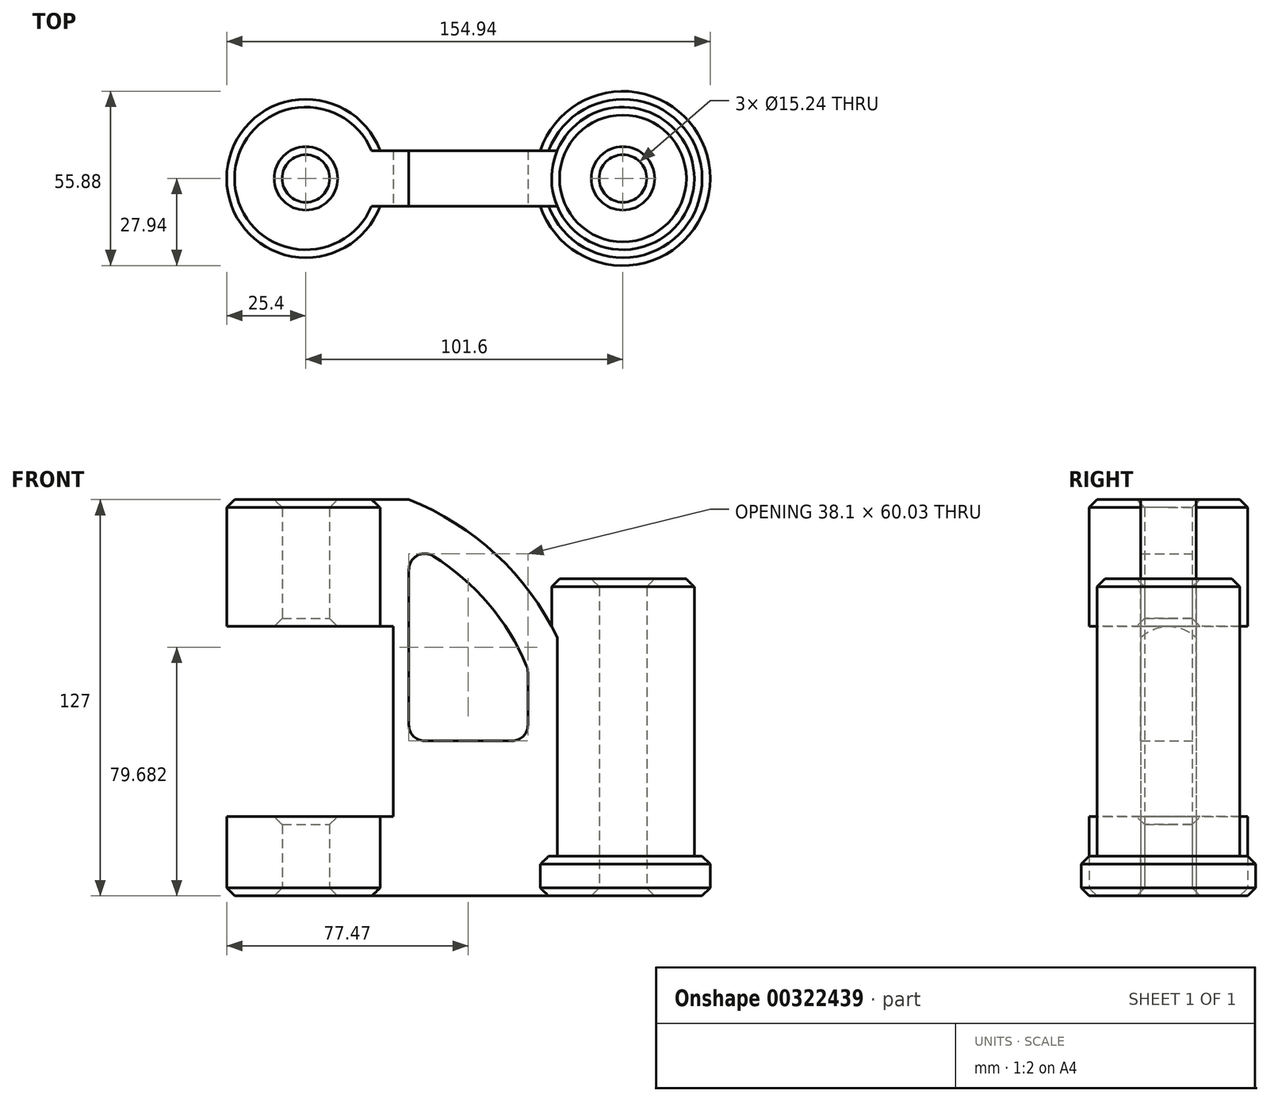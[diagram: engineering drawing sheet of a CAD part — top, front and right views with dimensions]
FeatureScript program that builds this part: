
annotation { "Feature Type Name" : "Feature", "Feature Type Description" : "" }
export const myFeature = defineFeature(function(context is Context, id is Id, definition is map)
    precondition{}
    {
        {
            var Q0;
            Q0=qCreatedBy(makeId("Top.planeOp"),FACE);
            var sketch = newSketch(context, id + "F0", { "sketchPlane" : qUnion([Q0])});
            skCircle(sketch, "E0", {"center": v(0, 0) * mm, "radius": 25.4 * mm});
            skCircle(sketch, "E1", {"center": v(0, 0) * mm, "radius": 7.62 * mm});
            skCircle(sketch, "E2", {"center": v(101.6, 0) * mm, "radius": 22.86 * mm});
            skCircle(sketch, "E3", {"center": v(101.6, 0) * mm, "radius": 7.62 * mm});
            skSolve(sketch);
        }
        {
            var Q0;
            Q0=makeQuery(id+"F0.imprint","IMPRINT",FACE,{"disambiguationData":[TD([[makeQuery(id+"F0.imprint","IMPRINT",EDGE,{"derivedFrom":sQuery(id+"F0.wireOp",EDGE,"E0")}),1.0]])]});
            extrude(context, id + "F1", {"entities" : qUnion([Q0]), "depth" : 127 * mm});
        }
        {
            var Q0;
            Q0=makeQuery(id+"F0.imprint","IMPRINT",FACE,{"disambiguationData":[TD([[makeQuery(id+"F0.imprint","IMPRINT",EDGE,{"derivedFrom":sQuery(id+"F0.wireOp",EDGE,"E2")}),1.0]])]});
            extrude(context, id + "F2", {"entities" : qUnion([Q0]), "depth" : 101.6 * mm});
        }
        {
            var Q0;
            Q0=qCreatedBy(makeId("Front.planeOp"),FACE);
            var sketch = newSketch(context, id + "F3", { "sketchPlane" : qUnion([Q0])});
            skLineSegment(sketch, "E4", {"start": v(20.32, 0) * mm, "end": v(20.32, 127) * mm});
            skLineSegment(sketch, "E5", {"start": v(20.32, 127) * mm, "end": v(33.02, 127) * mm});
            skArc(sketch, "E6", {"start": v(81.28, 81.28) * mm, "mid": v(61.58, 108.82) * mm, "end": v(33.02, 127) * mm});
            skLineSegment(sketch, "E7", {"start": v(81.28, 81.28) * mm, "end": v(81.28, 0) * mm});
            skLineSegment(sketch, "E8", {"start": v(81.28, 0) * mm, "end": v(20.32, 0) * mm});
            skArc(sketch, "E9.0", {"start": v(71.12, 72.77) * mm, "mid": v(55.88, 96.56) * mm, "end": v(33.02, 113.17) * mm});
            skLineSegment(sketch, "E10", {"start": v(33.02, 113.17) * mm, "end": v(33.02, 49.67) * mm});
            skLineSegment(sketch, "E11", {"start": v(33.02, 49.67) * mm, "end": v(71.12, 49.67) * mm});
            skLineSegment(sketch, "E12", {"start": v(71.12, 49.67) * mm, "end": v(71.12, 72.77) * mm});
            skSolve(sketch);
        }
        {
            var Q0;
            Q0=makeQuery(id+"F3.imprint","IMPRINT",FACE,{"disambiguationData":[TD([[makeQuery(id+"F3.imprint","IMPRINT",EDGE,{"derivedFrom":sQuery(id+"F3.wireOp",EDGE,"E4")}),-1.0]])]});
            extrude(context, id + "F4", {"entities" : qUnion([Q0]), "operationType" : NewBodyOperationType.ADD, "depth" : 17.78 * mm, "symmetric" : true});
        }
        {
            var Q0;
            Q0=qCreatedBy(makeId("Front.planeOp"),FACE);
            var sketch = newSketch(context, id + "F5", { "sketchPlane" : qUnion([Q0])});
            skLineSegment(sketch, "E13.bottom", {"start": v(-33.02, 86.36) * mm, "end": v(27.94, 86.36) * mm});
            skLineSegment(sketch, "E13.top", {"start": v(-33.02, 25.4) * mm, "end": v(27.94, 25.4) * mm});
            skLineSegment(sketch, "E13.left", {"start": v(-33.02, 86.36) * mm, "end": v(-33.02, 25.4) * mm});
            skLineSegment(sketch, "E13.right", {"start": v(27.94, 86.36) * mm, "end": v(27.94, 25.4) * mm});
            skSolve(sketch);
        }
        {
            var Q0;
            Q0=makeQuery(id+"F5.imprint","IMPRINT",FACE,{"disambiguationData":[TD([[makeQuery(id+"F5.imprint","IMPRINT",EDGE,{"derivedFrom":sQuery(id+"F5.wireOp",EDGE,"E13.bottom")}),-1.0]])]});
            extrude(context, id + "F6", {"entities" : qUnion([Q0]), "operationType" : NewBodyOperationType.REMOVE, "oppositeDirection" : true, "depth" : 101.6 * mm, "symmetric" : true});
        }
        {
            var Q0;
            Q0=makeQuery(id+"F4.opExtrude","SWEPT_EDGE",EDGE,{"disambiguationData":[OSD([sQuery(id+"F3.wireOp",EDGE,"E9.0"),sQuery(id+"F3.wireOp",EDGE,"E10")])]});
            var Q1;
            Q1=makeQuery(id+"F4.opExtrude","SWEPT_EDGE",EDGE,{"disambiguationData":[OSD([sQuery(id+"F3.wireOp",EDGE,"E10"),sQuery(id+"F3.wireOp",EDGE,"E11")])]});
            var Q2;
            Q2=makeQuery(id+"F4.opExtrude","SWEPT_EDGE",EDGE,{"disambiguationData":[OSD([sQuery(id+"F3.wireOp",EDGE,"E11"),sQuery(id+"F3.wireOp",EDGE,"E12")])]});
            var Q3;
            Q3=makeQuery(id+"F4.opExtrude","SWEPT_EDGE",EDGE,{"disambiguationData":[OSD([sQuery(id+"F3.wireOp",EDGE,"E9.0"),sQuery(id+"F3.wireOp",EDGE,"E12")])]});
            fillet(context, id + "F7", {"entities" : qUnion([Q0, Q1, Q2, Q3]), "radius" : 5.08 * mm, "tangentPropagation" : true, "allowEdgeOverflow" : false});
        }
        {
            var Q0;
            Q0=makeQuery(id+"F1.opExtrude","CAP_EDGE",EDGE,{"disambiguationData":[OSD([sQuery(id+"F0.wireOp",EDGE,"E0")])],"isStart":false});
            var Q1;
            Q1=makeQuery(id+"F1.opExtrude","CAP_EDGE",EDGE,{"disambiguationData":[OSD([sQuery(id+"F0.wireOp",EDGE,"E1")])],"isStart":false});
            var Q2;
            Q2=makeQuery(id+"F6.boolean.opBoolean","INTERSECT",EDGE,{"derivedFrom":[makeQuery(id+"F1.opExtrude","SWEPT_FACE",FACE,{"disambiguationData":[OSD([sQuery(id+"F0.wireOp",EDGE,"E1")])]}),makeQuery(id+"F6.opExtrude","SWEPT_FACE",FACE,{"disambiguationData":[OSD([sQuery(id+"F5.wireOp",EDGE,"E13.top")])]})]});
            var Q3;
            Q3=makeQuery(id+"F1.opExtrude","CAP_EDGE",EDGE,{"disambiguationData":[OSD([sQuery(id+"F0.wireOp",EDGE,"E0")])],"isStart":true});
            var Q4;
            Q4=makeQuery(id+"F6.boolean.opBoolean","INTERSECT",EDGE,{"derivedFrom":[makeQuery(id+"F1.opExtrude","SWEPT_FACE",FACE,{"disambiguationData":[OSD([sQuery(id+"F0.wireOp",EDGE,"E1")])]}),makeQuery(id+"F6.opExtrude","SWEPT_FACE",FACE,{"disambiguationData":[OSD([sQuery(id+"F5.wireOp",EDGE,"E13.bottom")])]})]});
            var Q5;
            Q5=makeQuery(id+"F1.opExtrude","CAP_EDGE",EDGE,{"disambiguationData":[OSD([sQuery(id+"F0.wireOp",EDGE,"E1")])],"isStart":true});
            chamfer(context, id + "F8", {"entities" : qUnion([Q0, Q1, Q2, Q3, Q4, Q5]), "width" : 2.54 * mm, "tangentPropagation" : true});
        }
        {
            var Q0;
            Q0=qCreatedBy(makeId("Top.planeOp"),FACE);
            var sketch = newSketch(context, id + "F9", { "sketchPlane" : qUnion([Q0])});
            skCircle(sketch, "E14.0", {"center": v(101.6, 0) * mm, "radius": 22.86 * mm});
            skCircle(sketch, "E15.0", {"center": v(101.6, 0) * mm, "radius": 27.94 * mm});
            skSolve(sketch);
        }
        {
            var Q0;
            Q0=makeQuery(id+"F9.imprint","IMPRINT",FACE,{"disambiguationData":[TD([[makeQuery(id+"F9.imprint","IMPRINT",EDGE,{"derivedFrom":sQuery(id+"F9.wireOp",EDGE,"E14.0")}),-1.0]])]});
            extrude(context, id + "F10", {"entities" : qUnion([Q0]), "operationType" : NewBodyOperationType.ADD, "depth" : 12.7 * mm});
        }
        {
            var Q0;
            Q0=makeQuery(id+"F2.opExtrude","CAP_EDGE",EDGE,{"disambiguationData":[OSD([sQuery(id+"F0.wireOp",EDGE,"E3")])],"isStart":true});
            var Q1;
            Q1=makeQuery(id+"F10.opExtrude","CAP_EDGE",EDGE,{"disambiguationData":[OSD([sQuery(id+"F9.wireOp",EDGE,"E15.0")])],"isStart":true});
            var Q2;
            Q2=makeQuery(id+"F2.opExtrude","CAP_EDGE",EDGE,{"disambiguationData":[OSD([sQuery(id+"F0.wireOp",EDGE,"E3")])],"isStart":false});
            var Q3;
            Q3=makeQuery(id+"F10.opExtrude","CAP_EDGE",EDGE,{"disambiguationData":[OSD([sQuery(id+"F9.wireOp",EDGE,"E15.0")])],"isStart":false});
            var Q4;
            Q4=makeQuery(id+"F2.opExtrude","CAP_EDGE",EDGE,{"disambiguationData":[OSD([sQuery(id+"F0.wireOp",EDGE,"E2")])],"isStart":false});
            chamfer(context, id + "F11", {"entities" : qUnion([Q0, Q1, Q2, Q3, Q4]), "width" : 2.54 * mm, "tangentPropagation" : true});
        }
    });
